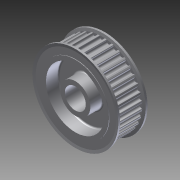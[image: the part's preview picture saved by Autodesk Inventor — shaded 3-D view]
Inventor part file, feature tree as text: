
AUTODESK INVENTOR PART (.ipt)
format: ipt  version: 2014 SP1 (Build 180222100, 222)  size: 1,036,800 bytes
history: native  units: in
note: dims shown in document units (in); Inventor stores cm internally (conversion verified against a paired STEP export)
features: mirror x1, other x1, imported_body x1
ambient origin geometry x8: Origin, YZ Plane, XZ Plane, XY Plane, X Axis, Y Axis, Z Axis, Center Point
bodies: Body1 (feature_tree)
feature tree (3):
  mirror  "Mirror1"
  other  "217-3232-STEP1"
  imported_body  "Base1"
